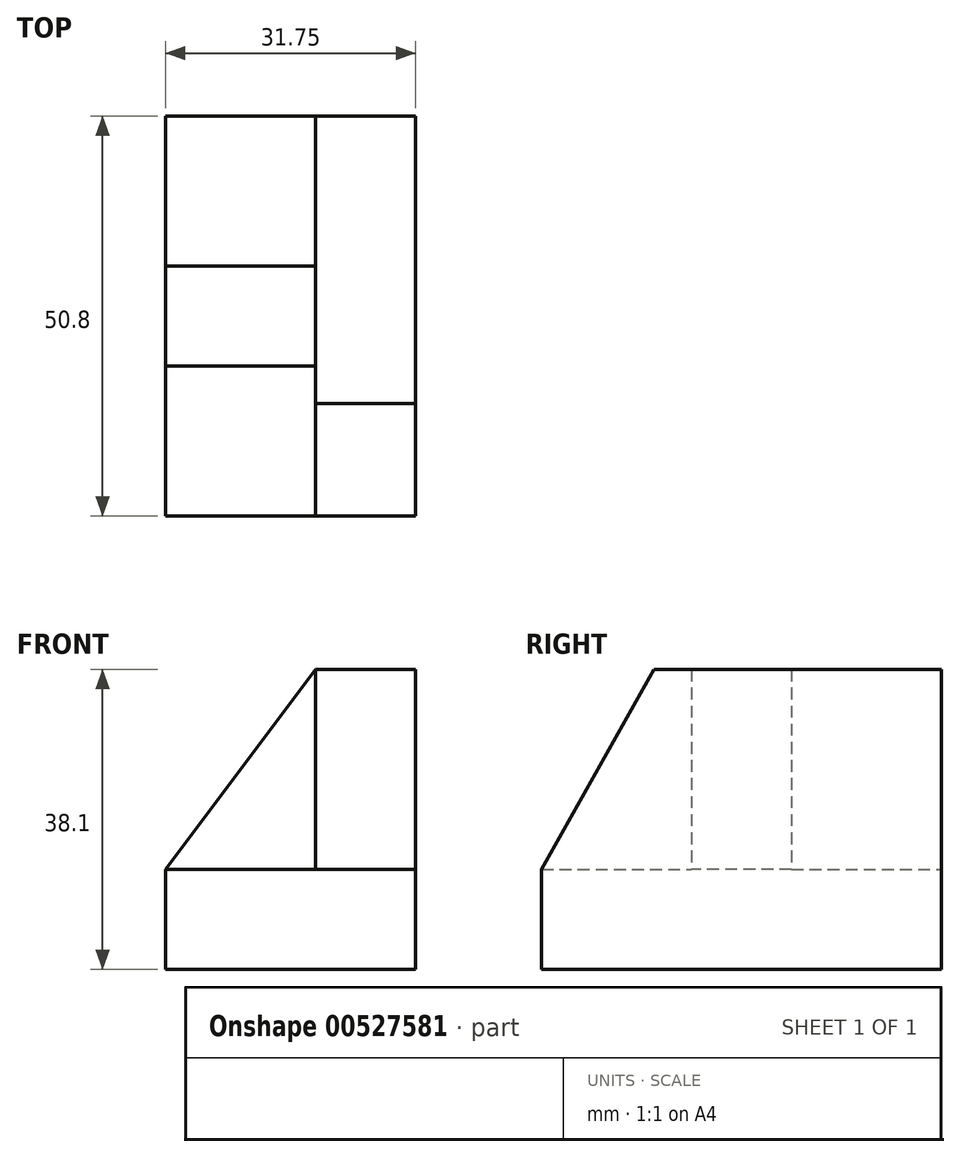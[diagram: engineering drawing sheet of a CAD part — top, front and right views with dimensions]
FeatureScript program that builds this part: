
annotation { "Feature Type Name" : "Feature", "Feature Type Description" : "" }
export const myFeature = defineFeature(function(context is Context, id is Id, definition is map)
    precondition{}
    {
        {
            var Q0;
            Q0=qCreatedBy(makeId("Front.planeOp"),FACE);
            var sketch = newSketch(context, id + "F0", { "sketchPlane" : qUnion([Q0])});
            skLineSegment(sketch, "E0", {"start": v(0, 0) * mm, "end": v(31.75, 0) * mm});
            skLineSegment(sketch, "E1", {"start": v(31.75, 0) * mm, "end": v(31.75, 38.1) * mm});
            skLineSegment(sketch, "E2", {"start": v(31.75, 38.1) * mm, "end": v(19.05, 38.1) * mm});
            skLineSegment(sketch, "E3", {"start": v(19.05, 38.1) * mm, "end": v(19.05, 12.7) * mm});
            skLineSegment(sketch, "E4", {"start": v(19.05, 12.7) * mm, "end": v(0, 12.7) * mm});
            skLineSegment(sketch, "E5", {"start": v(0, 12.7) * mm, "end": v(0, 0) * mm});
            skSolve(sketch);
        }
        {
            var Q0;
            Q0=makeQuery(id+"F0.imprint","IMPRINT",FACE,{"disambiguationData":[TD([[makeQuery(id+"F0.imprint","IMPRINT",EDGE,{"derivedFrom":sQuery(id+"F0.wireOp",EDGE,"E0")}),1.0]])]});
            extrude(context, id + "F1", {"entities" : qUnion([Q0]), "depth" : 50.8 * mm, "offsetDistance" : 25.4 * mm});
        }
        {
            var Q0;
            Q0=makeQuery(id+"F1.opExtrude","SWEPT_FACE",FACE,{"disambiguationData":[OSD([sQuery(id+"F0.wireOp",EDGE,"E3")])]});
            var sketch = newSketch(context, id + "F2", { "sketchPlane" : qUnion([Q0])});
            skLineSegment(sketch, "E6", {"start": v(50.8, 12.7) * mm, "end": v(36.52, 38.1) * mm});
            skSolve(sketch);
        }
        {
            var Q0;
            {var subQ0=sQuery(id+"F2.wireOp",EDGE,"E6");Q0=makeQuery(id+"F2.imprint","IMPRINT",FACE,{"disambiguationData":[TD([[makeQuery(id+"F2.imprint","IMPRINT",EDGE,{"derivedFrom":subQ0}),-1.0]])]});}
            extrude(context, id + "F3", {"entities" : qUnion([Q0]), "operationType" : NewBodyOperationType.REMOVE, "oppositeDirection" : true, "depth" : 25.4 * mm, "offsetDistance" : 25.4 * mm});
        }
        {
            var Q0;
            Q0=makeQuery(id+"F1.opExtrude","SWEPT_FACE",FACE,{"disambiguationData":[OSD([sQuery(id+"F0.wireOp",EDGE,"E3")])]});
            var sketch = newSketch(context, id + "F4", { "sketchPlane" : qUnion([Q0])});
            skLineSegment(sketch, "E7", {"start": v(19.05, 38.1) * mm, "end": v(19.05, 12.7) * mm});
            skLineSegment(sketch, "E8", {"start": v(31.75, 38.1) * mm, "end": v(31.75, 12.7) * mm});
            skSolve(sketch);
        }
        {
            var Q0;
            {var subQ0=sQuery(id+"F4.wireOp",EDGE,"E7");Q0=makeQuery(id+"F4.imprint","IMPRINT",FACE,{"disambiguationData":[TD([[makeQuery(id+"F4.imprint","IMPRINT",EDGE,{"derivedFrom":subQ0}),1.0]])]});}
            extrude(context, id + "F5", {"entities" : qUnion([Q0]), "operationType" : NewBodyOperationType.ADD, "depth" : 19.05 * mm, "offsetDistance" : 25.4 * mm});
        }
        {
            var Q0;
            Q0=makeQuery(id+"F5.opExtrude","SWEPT_FACE",FACE,{"disambiguationData":[OSD([sQuery(id+"F4.wireOp",EDGE,"E8")])]});
            var sketch = newSketch(context, id + "F6", { "sketchPlane" : qUnion([Q0])});
            skLineSegment(sketch, "E9", {"start": v(19.05, 38.1) * mm, "end": v(0, 12.7) * mm});
            skSolve(sketch);
        }
        {
            var Q0;
            Q0=makeQuery(id+"F6.imprint","IMPRINT",FACE,{"disambiguationData":[TD([[makeQuery(id+"F6.imprint","IMPRINT",EDGE,{"derivedFrom":sQuery(id+"F6.wireOp",EDGE,"E9")}),-1.0]])]});
            extrude(context, id + "F7", {"entities" : qUnion([Q0]), "operationType" : NewBodyOperationType.REMOVE, "oppositeDirection" : true, "depth" : 25.4 * mm, "offsetDistance" : 25.4 * mm});
        }
    });
